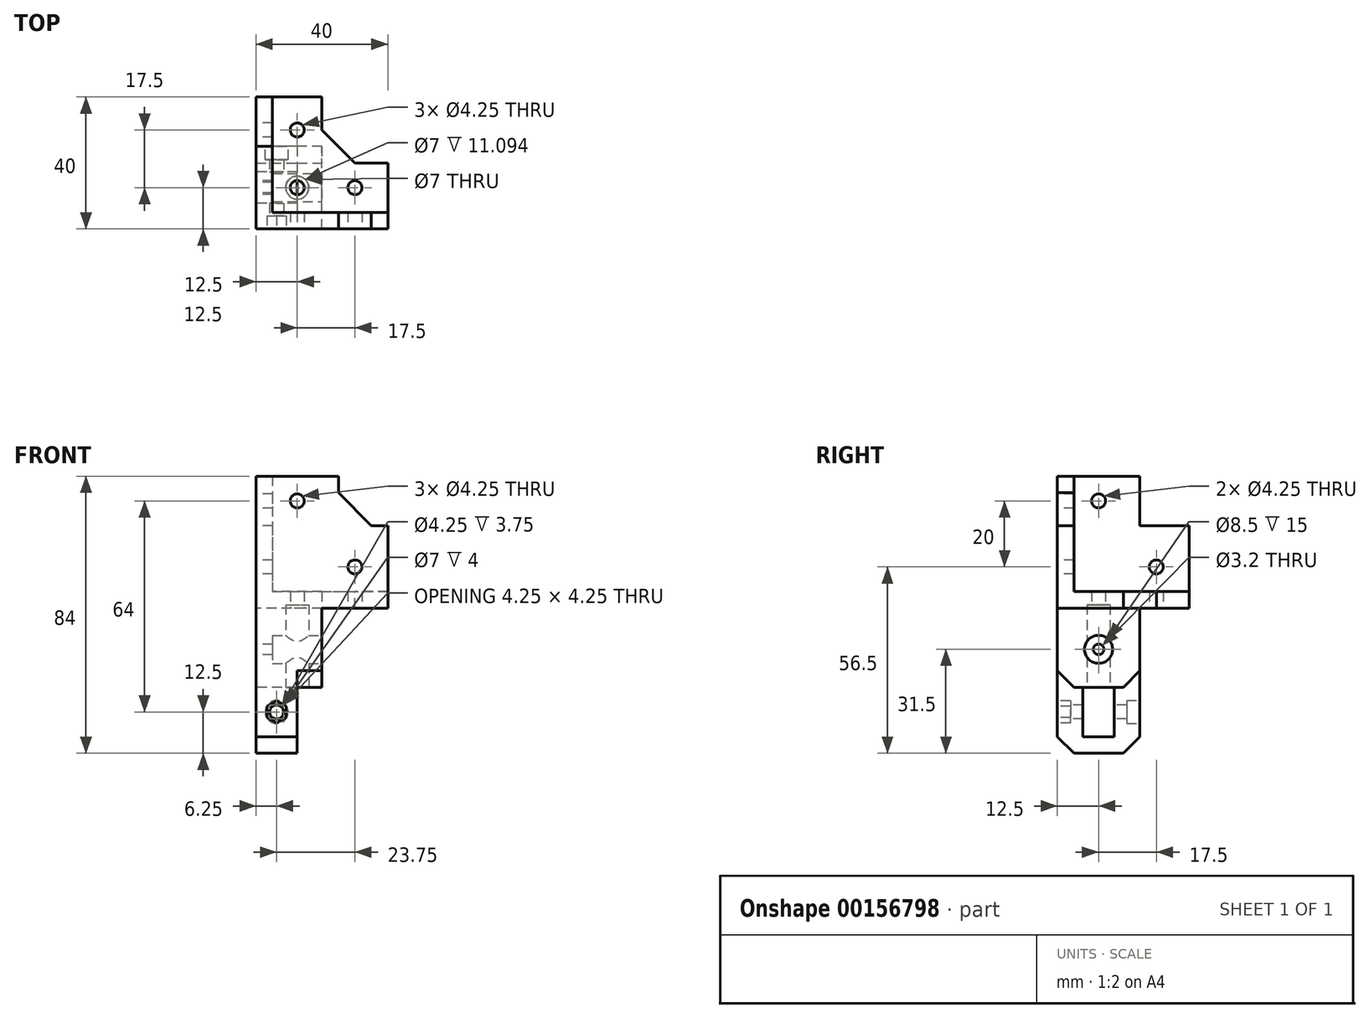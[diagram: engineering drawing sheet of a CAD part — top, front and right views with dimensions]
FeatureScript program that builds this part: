
annotation { "Feature Type Name" : "Feature", "Feature Type Description" : "" }
export const myFeature = defineFeature(function(context is Context, id is Id, definition is map)
    precondition{}
    {
        {
            var Q0;
            Q0=qCreatedBy(makeId("Top.planeOp"),FACE);
            var sketch = newSketch(context, id + "F0", { "sketchPlane" : qUnion([Q0])});
            skLineSegment(sketch, "E0", {"start": v(0, 40) * mm, "end": v(-20, 40) * mm});
            skLineSegment(sketch, "E1", {"start": v(-20, 40) * mm, "end": v(-20, 0) * mm});
            skLineSegment(sketch, "E2", {"start": v(-20, 0) * mm, "end": v(20, 0) * mm});
            skLineSegment(sketch, "E3", {"start": v(20, 0) * mm, "end": v(20, 20) * mm});
            skLineSegment(sketch, "E4", {"start": v(20, 20) * mm, "end": v(0, 20) * mm});
            skLineSegment(sketch, "E5", {"start": v(0, 20) * mm, "end": v(0, 40) * mm});
            skCircle(sketch, "E6", {"center": v(-7.5, 30) * mm, "radius": 2.12 * mm});
            skCircle(sketch, "E7", {"center": v(10, 12.5) * mm, "radius": 2.12 * mm});
            skCircle(sketch, "E8", {"center": v(-7.5, 12.5) * mm, "radius": 2.12 * mm});
            skSolve(sketch);
        }
        {
            var Q0;
            Q0=qSketchRegion(id+"F0",true);
            extrude(context, id + "F1", {"entities" : qUnion([Q0]), "depth" : 5 * mm});
        }
        {
            var Q0;
            Q0=makeQuery(id+"F1.opExtrude","CAP_FACE",FACE,{"disambiguationData":[OSD([sQuery(id+"F0.wireOp",EDGE,"E0"),sQuery(id+"F0.wireOp",EDGE,"E1"),sQuery(id+"F0.wireOp",EDGE,"E2"),sQuery(id+"F0.wireOp",EDGE,"E3"),sQuery(id+"F0.wireOp",EDGE,"E4"),sQuery(id+"F0.wireOp",EDGE,"E5"),sQuery(id+"F0.wireOp",EDGE,"E6"),sQuery(id+"F0.wireOp",EDGE,"E7")])],"isStart":false});
            var sketch = newSketch(context, id + "F2", { "sketchPlane" : qUnion([Q0])});
            skLineSegment(sketch, "E9", {"start": v(-20, 40) * mm, "end": v(-15, 40) * mm});
            skLineSegment(sketch, "E10", {"start": v(-15, 40) * mm, "end": v(-15, 5) * mm});
            skLineSegment(sketch, "E11", {"start": v(-15, 5) * mm, "end": v(20, 5) * mm});
            skLineSegment(sketch, "E12", {"start": v(20, 5) * mm, "end": v(20, 0) * mm});
            skLineSegment(sketch, "E13", {"start": v(20, 0) * mm, "end": v(-20, 0) * mm});
            skLineSegment(sketch, "E14", {"start": v(-20, 0) * mm, "end": v(-20, 40) * mm});
            skSolve(sketch);
        }
        {
            var Q0;
            Q0=qSketchRegion(id+"F2",true);
            extrude(context, id + "F3", {"entities" : qUnion([Q0]), "operationType" : NewBodyOperationType.ADD, "depth" : 20 * mm});
        }
        {
            var Q0;
            Q0=makeQuery(id+"F3.opExtrude","CAP_FACE",FACE,{"disambiguationData":[OSD([sQuery(id+"F2.wireOp",EDGE,"E9"),sQuery(id+"F2.wireOp",EDGE,"E10"),sQuery(id+"F2.wireOp",EDGE,"E11"),sQuery(id+"F2.wireOp",EDGE,"E12"),sQuery(id+"F2.wireOp",EDGE,"E13"),sQuery(id+"F2.wireOp",EDGE,"E14")])],"isStart":false});
            var sketch = newSketch(context, id + "F4", { "sketchPlane" : qUnion([Q0])});
            skLineSegment(sketch, "E15", {"start": v(-15, 25) * mm, "end": v(-20, 25) * mm});
            skLineSegment(sketch, "E16", {"start": v(-20, 25) * mm, "end": v(-20, 0) * mm});
            skLineSegment(sketch, "E17", {"start": v(-20, 0) * mm, "end": v(5, 0) * mm});
            skLineSegment(sketch, "E18", {"start": v(5, 0) * mm, "end": v(5, 5) * mm});
            skLineSegment(sketch, "E19", {"start": v(5, 5) * mm, "end": v(-15, 5) * mm});
            skLineSegment(sketch, "E20", {"start": v(-15, 5) * mm, "end": v(-15, 25) * mm});
            skSolve(sketch);
        }
        {
            var Q0;
            Q0=qSketchRegion(id+"F4",true);
            extrude(context, id + "F5", {"entities" : qUnion([Q0]), "operationType" : NewBodyOperationType.ADD, "depth" : 15 * mm});
        }
        {
            var Q0;
            Q0=makeQuery(id+"F1.opExtrude","SWEPT_EDGE",EDGE,{"disambiguationData":[OSD([sQuery(id+"F0.wireOp",EDGE,"E4"),sQuery(id+"F0.wireOp",EDGE,"E5")])]});
            var Q1;
            Q1=makeQuery(id+"F5.opExtrude","CAP_EDGE",EDGE,{"disambiguationData":[OSD([sQuery(id+"F4.wireOp",EDGE,"E15")])],"isStart":true});
            var Q2;
            Q2=makeQuery(id+"F5.opExtrude","CAP_EDGE",EDGE,{"disambiguationData":[OSD([sQuery(id+"F4.wireOp",EDGE,"E18")])],"isStart":true});
            chamfer(context, id + "F6", {"entities" : qUnion([Q0, Q1, Q2]), "width" : 10 * mm, "tangentPropagation" : true});
        }
        {
            var Q0;
            Q0=makeQuery(id+"F5.boolean.opBoolean","MERGE",FACE,{"derivedFrom":[makeQuery(id+"F3.boolean.opBoolean","MERGE",FACE,{"derivedFrom":[makeQuery(id+"F1.opExtrude","SWEPT_FACE",FACE,{"disambiguationData":[OSD([sQuery(id+"F0.wireOp",EDGE,"E2")])]}),makeQuery(id+"F3.opExtrude","SWEPT_FACE",FACE,{"disambiguationData":[OSD([sQuery(id+"F2.wireOp",EDGE,"E13")])]})]}),makeQuery(id+"F5.opExtrude","SWEPT_FACE",FACE,{"disambiguationData":[OSD([sQuery(id+"F4.wireOp",EDGE,"E17")])]})]});
            var sketch = newSketch(context, id + "F7", { "sketchPlane" : qUnion([Q0])});
            skCircle(sketch, "E21", {"center": v(-7.5, 32.5) * mm, "radius": 2.12 * mm});
            skCircle(sketch, "E22", {"center": v(10, 12.5) * mm, "radius": 2.12 * mm});
            skSolve(sketch);
        }
        {
            var Q0;
            Q0=qSketchRegion(id+"F7",true);
            extrude(context, id + "F8", {"entities" : qUnion([Q0]), "operationType" : NewBodyOperationType.REMOVE, "oppositeDirection" : true, "depth" : 5 * mm});
        }
        {
            var Q0;
            Q0=makeQuery(id+"F5.boolean.opBoolean","MERGE",FACE,{"derivedFrom":[makeQuery(id+"F3.boolean.opBoolean","MERGE",FACE,{"derivedFrom":[makeQuery(id+"F1.opExtrude","SWEPT_FACE",FACE,{"disambiguationData":[OSD([sQuery(id+"F0.wireOp",EDGE,"E1")])]}),makeQuery(id+"F3.opExtrude","SWEPT_FACE",FACE,{"disambiguationData":[OSD([sQuery(id+"F2.wireOp",EDGE,"E14")])]})]}),makeQuery(id+"F5.opExtrude","SWEPT_FACE",FACE,{"disambiguationData":[OSD([sQuery(id+"F4.wireOp",EDGE,"E16")])]})]});
            var sketch = newSketch(context, id + "F9", { "sketchPlane" : qUnion([Q0])});
            skCircle(sketch, "E23", {"center": v(-12.5, 32.5) * mm, "radius": 2.12 * mm});
            skCircle(sketch, "E24", {"center": v(-30, 12.5) * mm, "radius": 2.12 * mm});
            skSolve(sketch);
        }
        {
            var Q0;
            Q0=qSketchRegion(id+"F9",true);
            extrude(context, id + "F10", {"entities" : qUnion([Q0]), "operationType" : NewBodyOperationType.REMOVE, "oppositeDirection" : true, "depth" : 5 * mm});
        }
        {
            var Q0;
            Q0=makeQuery(id+"F1.opExtrude","CAP_FACE",FACE,{"disambiguationData":[OSD([sQuery(id+"F0.wireOp",EDGE,"E0"),sQuery(id+"F0.wireOp",EDGE,"E1"),sQuery(id+"F0.wireOp",EDGE,"E2"),sQuery(id+"F0.wireOp",EDGE,"E3"),sQuery(id+"F0.wireOp",EDGE,"E4"),sQuery(id+"F0.wireOp",EDGE,"E5"),sQuery(id+"F0.wireOp",EDGE,"E6"),sQuery(id+"F0.wireOp",EDGE,"E7"),sQuery(id+"F0.wireOp",EDGE,"E8")])],"isStart":true});
            var sketch = newSketch(context, id + "F11", { "sketchPlane" : qUnion([Q0])});
            skLineSegment(sketch, "E25.bottom", {"start": v(20, -20) * mm, "end": v(-20, -20) * mm});
            skLineSegment(sketch, "E25.top", {"start": v(20, 0) * mm, "end": v(-20, 0) * mm});
            skLineSegment(sketch, "E25.left", {"start": v(20, -20) * mm, "end": v(20, 0) * mm});
            skLineSegment(sketch, "E25.right", {"start": v(-20, -20) * mm, "end": v(-20, 0) * mm});
            skPoint(sketch, "E25.middle", {"position": v(0, -10) * mm});
            skPoint(sketch, "E26.visualSharp", {"position": v(-20, 0) * mm});
            skLineSegment(sketch, "E26.filletArc", {"start": v(-20, 0) * mm, "end": v(-20, 0) * mm});
            skCircle(sketch, "E27", {"center": v(10, -12.5) * mm, "radius": 2.12 * mm});
            skCircle(sketch, "E28", {"center": v(-7.5, -12.5) * mm, "radius": 2.12 * mm});
            skSolve(sketch);
        }
        {
            var Q0;
            Q0=qSketchRegion(id+"F11",true);
            extrude(context, id + "F12", {"entities" : qUnion([Q0]), "operationType" : NewBodyOperationType.ADD, "depth" : 24 * mm});
        }
        {
            var Q0;
            Q0=makeQuery(id+"F12.boolean.opBoolean","MERGE",FACE,{"derivedFrom":[makeQuery(id+"F1.opExtrude","SWEPT_FACE",FACE,{"disambiguationData":[OSD([sQuery(id+"F0.wireOp",EDGE,"E4")])]}),makeQuery(id+"F12.opExtrude","SWEPT_FACE",FACE,{"disambiguationData":[OSD([sQuery(id+"F11.wireOp",EDGE,"E25.bottom")])]})]});
            var sketch = newSketch(context, id + "F13", { "sketchPlane" : qUnion([Q0])});
            skLineSegment(sketch, "E29", {"start": v(20, -11.5) * mm, "end": v(20, -24) * mm});
            skLineSegment(sketch, "E30", {"start": v(20, -24) * mm, "end": v(7.5, -24) * mm});
            skPoint(sketch, "E31.orphan", {"position": v(7.5, -24) * mm});
            skCircle(sketch, "E32", {"center": v(7.5, -11.5) * mm, "radius": 4.15 * mm, "construction": true});
            skLineSegment(sketch, "E33", {"start": v(0, -11.5) * mm, "end": v(0, 0) * mm});
            skLineSegment(sketch, "E34", {"start": v(0, 0) * mm, "end": v(-20, 0) * mm});
            skLineSegment(sketch, "E35", {"start": v(-20, 0) * mm, "end": v(-20, -24) * mm});
            skLineSegment(sketch, "E36", {"start": v(-20, -24) * mm, "end": v(7.5, -24) * mm});
            skLineSegment(sketch, "E37", {"start": v(0, -11.5) * mm, "end": v(0, -24) * mm});
            skSolve(sketch);
        }
        {
            var Q0;
            Q0=qSketchRegion(id+"F13",true);
            extrude(context, id + "F14", {"entities" : qUnion([Q0]), "operationType" : NewBodyOperationType.REMOVE, "oppositeDirection" : true, "depth" : 25 * mm});
        }
        {
            var Q0;
            Q0=makeQuery(id+"F14.boolean.opBoolean","COPY",FACE,{"derivedFrom":makeQuery(id+"F14.opExtrude","SWEPT_FACE",FACE,{"disambiguationData":[OSD([sQuery(id+"F13.wireOp",EDGE,"E33"),sQuery(id+"F13.wireOp",EDGE,"E37")])]})});
            var sketch = newSketch(context, id + "F15", { "sketchPlane" : qUnion([Q0])});
            skCircle(sketch, "E38", {"center": v(12.5, -12.5) * mm, "radius": 4.25 * mm});
            skSolve(sketch);
        }
        {
            var Q0;
            Q0=qSketchRegion(id+"F15",true);
            extrude(context, id + "F16", {"entities" : qUnion([Q0]), "operationType" : NewBodyOperationType.REMOVE, "oppositeDirection" : true, "depth" : 20 * mm});
        }
        {
            var Q0;
            Q0=makeQuery(id+"F12.opExtrude","CAP_FACE",FACE,{"disambiguationData":[OSD([sQuery(id+"F11.wireOp",EDGE,"E25.bottom"),sQuery(id+"F11.wireOp",EDGE,"E25.top"),sQuery(id+"F11.wireOp",EDGE,"E25.left"),sQuery(id+"F11.wireOp",EDGE,"E25.right"),sQuery(id+"F11.wireOp",EDGE,"E27"),sQuery(id+"F11.wireOp",EDGE,"E28")])],"isStart":false});
            var sketch = newSketch(context, id + "F17", { "sketchPlane" : qUnion([Q0])});
            skCircle(sketch, "E39", {"center": v(-7.5, -12.5) * mm, "radius": 3.5 * mm});
            skSolve(sketch);
        }
        {
            var Q0;
            Q0=qSketchRegion(id+"F17",true);
            extrude(context, id + "F18", {"entities" : qUnion([Q0]), "operationType" : NewBodyOperationType.REMOVE, "oppositeDirection" : true, "depth" : 25 * mm});
        }
        {
            var Q0;
            {var subQ1=sQuery(id+"F11.wireOp",EDGE,"E25.bottom");var subQ2=sQuery(id+"F0.wireOp",EDGE,"E1");var subQ3=sQuery(id+"F0.wireOp",EDGE,"E4");Q0=makeQuery(id+"F14.boolean.opBoolean","SPLIT",FACE,{"disambiguationData":[TD([makeQuery(id+"F1.opExtrude","SWEPT_FACE",FACE,{"disambiguationData":[OSD([subQ2])]})])],"derivedFrom":makeQuery(id+"F12.boolean.opBoolean","MERGE",FACE,{"derivedFrom":[makeQuery(id+"F1.opExtrude","SWEPT_FACE",FACE,{"disambiguationData":[OSD([subQ3])]}),makeQuery(id+"F12.opExtrude","SWEPT_FACE",FACE,{"disambiguationData":[OSD([subQ1])]})]})});}
            var sketch = newSketch(context, id + "F19", { "sketchPlane" : qUnion([Q0])});
            skLineSegment(sketch, "E40.bottom", {"start": v(0, 0) * mm, "end": v(20, 0) * mm});
            skLineSegment(sketch, "E40.top", {"start": v(0, -24) * mm, "end": v(20, -24) * mm});
            skLineSegment(sketch, "E40.left", {"start": v(0, 0) * mm, "end": v(0, -24) * mm});
            skLineSegment(sketch, "E40.right", {"start": v(20, 0) * mm, "end": v(20, -24) * mm});
            skSolve(sketch);
        }
        {
            var Q0;
            Q0=qSketchRegion(id+"F19",true);
            extrude(context, id + "F20", {"entities" : qUnion([Q0]), "operationType" : NewBodyOperationType.ADD, "depth" : 5 * mm});
        }
        {
            var Q0;
            Q0=makeQuery(id+"F20.boolean.opBoolean","MERGE",FACE,{"derivedFrom":[makeQuery(id+"F12.boolean.opBoolean","MERGE",FACE,{"derivedFrom":[makeQuery(id+"F5.boolean.opBoolean","MERGE",FACE,{"derivedFrom":[makeQuery(id+"F3.boolean.opBoolean","MERGE",FACE,{"derivedFrom":[makeQuery(id+"F1.opExtrude","SWEPT_FACE",FACE,{"disambiguationData":[OSD([sQuery(id+"F0.wireOp",EDGE,"E1")])]}),makeQuery(id+"F3.opExtrude","SWEPT_FACE",FACE,{"disambiguationData":[OSD([sQuery(id+"F2.wireOp",EDGE,"E14")])]})]}),makeQuery(id+"F5.opExtrude","SWEPT_FACE",FACE,{"disambiguationData":[OSD([sQuery(id+"F4.wireOp",EDGE,"E16")])]})]}),makeQuery(id+"F12.opExtrude","SWEPT_FACE",FACE,{"disambiguationData":[OSD([sQuery(id+"F11.wireOp",EDGE,"E25.right")])]})]}),makeQuery(id+"F20.opExtrude","SWEPT_FACE",FACE,{"disambiguationData":[OSD([sQuery(id+"F19.wireOp",EDGE,"E40.right")])]})]});
            var sketch = newSketch(context, id + "F21", { "sketchPlane" : qUnion([Q0])});
            skLineSegment(sketch, "E41", {"start": v(-25, -24) * mm, "end": v(-25, -44) * mm});
            skLineSegment(sketch, "E42", {"start": v(-25, -44) * mm, "end": v(0, -44) * mm});
            skLineSegment(sketch, "E43", {"start": v(0, -44) * mm, "end": v(0, -24) * mm});
            skLineSegment(sketch, "E44", {"start": v(0, -24) * mm, "end": v(-7.75, -24) * mm});
            skLineSegment(sketch, "E45", {"start": v(-7.75, -24) * mm, "end": v(-7.75, -39) * mm});
            skLineSegment(sketch, "E46", {"start": v(-7.75, -39) * mm, "end": v(-17.25, -39) * mm});
            skLineSegment(sketch, "E47", {"start": v(-17.25, -39) * mm, "end": v(-17.25, -24) * mm});
            skLineSegment(sketch, "E48", {"start": v(-17.25, -24) * mm, "end": v(-25, -24) * mm});
            skSolve(sketch);
        }
        {
            var Q0;
            Q0=qSketchRegion(id+"F21",true);
            extrude(context, id + "F22", {"entities" : qUnion([Q0]), "operationType" : NewBodyOperationType.ADD, "oppositeDirection" : true, "depth" : 12.5 * mm});
        }
        {
            var Q0;
            Q0=makeQuery(id+"F22.opExtrude","SWEPT_EDGE",EDGE,{"disambiguationData":[OSD([sQuery(id+"F21.wireOp",EDGE,"E41"),sQuery(id+"F21.wireOp",EDGE,"E42")])]});
            var Q1;
            Q1=makeQuery(id+"F22.opExtrude","SWEPT_EDGE",EDGE,{"disambiguationData":[OSD([sQuery(id+"F21.wireOp",EDGE,"E42"),sQuery(id+"F21.wireOp",EDGE,"E43")])]});
            var Q2;
            Q2=makeQuery(id+"F12.opExtrude","CAP_EDGE",EDGE,{"disambiguationData":[OSD([sQuery(id+"F11.wireOp",EDGE,"E25.top")])],"isStart":false});
            var Q3;
            Q3=makeQuery(id+"F20.opExtrude","CAP_EDGE",EDGE,{"disambiguationData":[OSD([sQuery(id+"F19.wireOp",EDGE,"E40.top")])],"isStart":false});
            var Q4;
            Q4=makeQuery(id+"F20.opExtrude","CAP_EDGE",EDGE,{"disambiguationData":[OSD([sQuery(id+"F19.wireOp",EDGE,"E40.bottom")])],"isStart":false});
            chamfer(context, id + "F23", {"entities" : qUnion([Q0, Q1, Q2, Q3, Q4]), "width" : 5 * mm, "tangentPropagation" : true});
        }
        {
            var Q0;
            Q0=makeQuery(id+"F23.opChamfer","SPLIT",FACE,{"disambiguationData":[OD(1.0)],"derivedFrom":makeQuery(id+"F14.boolean.opBoolean","MERGE",FACE,{"derivedFrom":[makeQuery(id+"F1.opExtrude","CAP_FACE",FACE,{"disambiguationData":[OSD([sQuery(id+"F0.wireOp",EDGE,"E0"),sQuery(id+"F0.wireOp",EDGE,"E1"),sQuery(id+"F0.wireOp",EDGE,"E2"),sQuery(id+"F0.wireOp",EDGE,"E3"),sQuery(id+"F0.wireOp",EDGE,"E4"),sQuery(id+"F0.wireOp",EDGE,"E5"),sQuery(id+"F0.wireOp",EDGE,"E6"),sQuery(id+"F0.wireOp",EDGE,"E7"),sQuery(id+"F0.wireOp",EDGE,"E8")])],"isStart":true}),makeQuery(id+"F14.opExtrude","SWEPT_FACE",FACE,{"disambiguationData":[OSD([sQuery(id+"F13.wireOp",EDGE,"E34")])]})]})});
            var sketch = newSketch(context, id + "F24", { "sketchPlane" : qUnion([Q0])});
            skCircle(sketch, "E49", {"center": v(-7.5, -30) * mm, "radius": 3.5 * mm});
            skSolve(sketch);
        }
        {
            var Q0;
            Q0=qSketchRegion(id+"F24",true);
            extrude(context, id + "F25", {"entities" : qUnion([Q0]), "operationType" : NewBodyOperationType.REMOVE, "endBound" : BoundingType.THROUGH_ALL, "depth" : 25 * mm});
        }
        {
            var Q0;
            Q0=makeQuery(id+"F22.boolean.opBoolean","MERGE",FACE,{"derivedFrom":[makeQuery(id+"F20.boolean.opBoolean","MERGE",FACE,{"derivedFrom":[makeQuery(id+"F12.boolean.opBoolean","MERGE",FACE,{"derivedFrom":[makeQuery(id+"F5.boolean.opBoolean","MERGE",FACE,{"derivedFrom":[makeQuery(id+"F3.boolean.opBoolean","MERGE",FACE,{"derivedFrom":[makeQuery(id+"F1.opExtrude","SWEPT_FACE",FACE,{"disambiguationData":[OSD([sQuery(id+"F0.wireOp",EDGE,"E1")])]}),makeQuery(id+"F3.opExtrude","SWEPT_FACE",FACE,{"disambiguationData":[OSD([sQuery(id+"F2.wireOp",EDGE,"E14")])]})]}),makeQuery(id+"F5.opExtrude","SWEPT_FACE",FACE,{"disambiguationData":[OSD([sQuery(id+"F4.wireOp",EDGE,"E16")])]})]}),makeQuery(id+"F12.opExtrude","SWEPT_FACE",FACE,{"disambiguationData":[OSD([sQuery(id+"F11.wireOp",EDGE,"E25.right")])]})]}),makeQuery(id+"F20.opExtrude","SWEPT_FACE",FACE,{"disambiguationData":[OSD([sQuery(id+"F19.wireOp",EDGE,"E40.right")])]})]}),makeQuery(id+"F22.opExtrude","CAP_FACE",FACE,{"disambiguationData":[OSD([sQuery(id+"F21.wireOp",EDGE,"E41"),sQuery(id+"F21.wireOp",EDGE,"E42"),sQuery(id+"F21.wireOp",EDGE,"E43"),sQuery(id+"F21.wireOp",EDGE,"E44"),sQuery(id+"F21.wireOp",EDGE,"E45"),sQuery(id+"F21.wireOp",EDGE,"E46"),sQuery(id+"F21.wireOp",EDGE,"E47"),sQuery(id+"F21.wireOp",EDGE,"E48")])],"isStart":true})]});
            var sketch = newSketch(context, id + "F26", { "sketchPlane" : qUnion([Q0])});
            skCircle(sketch, "E50", {"center": v(-12.5, -12.5) * mm, "radius": 4.25 * mm});
            skCircle(sketch, "E51", {"center": v(-12.5, -12.5) * mm, "radius": 1.6 * mm});
            skSolve(sketch);
        }
        {
            var Q0;
            Q0=qSketchRegion(id+"F26",true);
            extrude(context, id + "F27", {"entities" : qUnion([Q0]), "operationType" : NewBodyOperationType.ADD, "oppositeDirection" : true, "depth" : 5 * mm});
        }
        {
            var Q0;
            Q0=makeQuery(id+"F22.boolean.opBoolean","MERGE",FACE,{"derivedFrom":[makeQuery(id+"F12.boolean.opBoolean","MERGE",FACE,{"derivedFrom":[makeQuery(id+"F5.boolean.opBoolean","MERGE",FACE,{"derivedFrom":[makeQuery(id+"F3.boolean.opBoolean","MERGE",FACE,{"derivedFrom":[makeQuery(id+"F1.opExtrude","SWEPT_FACE",FACE,{"disambiguationData":[OSD([sQuery(id+"F0.wireOp",EDGE,"E2")])]}),makeQuery(id+"F3.opExtrude","SWEPT_FACE",FACE,{"disambiguationData":[OSD([sQuery(id+"F2.wireOp",EDGE,"E13")])]})]}),makeQuery(id+"F5.opExtrude","SWEPT_FACE",FACE,{"disambiguationData":[OSD([sQuery(id+"F4.wireOp",EDGE,"E17")])]})]}),makeQuery(id+"F12.opExtrude","SWEPT_FACE",FACE,{"disambiguationData":[OSD([sQuery(id+"F11.wireOp",EDGE,"E25.top")])]})]}),makeQuery(id+"F22.opExtrude","SWEPT_FACE",FACE,{"disambiguationData":[OSD([sQuery(id+"F21.wireOp",EDGE,"E43")])]})]});
            var sketch = newSketch(context, id + "F28", { "sketchPlane" : qUnion([Q0])});
            skCircle(sketch, "E52", {"center": v(-13.75, -31.5) * mm, "radius": 2.12 * mm});
            skSolve(sketch);
        }
        {
            var Q0;
            Q0=qSketchRegion(id+"F28",true);
            extrude(context, id + "F29", {"entities" : qUnion([Q0]), "operationType" : NewBodyOperationType.REMOVE, "endBound" : BoundingType.THROUGH_ALL, "oppositeDirection" : true, "depth" : 25 * mm});
        }
        {
            var Q0;
            Q0=makeQuery(id+"F22.boolean.opBoolean","MERGE",FACE,{"derivedFrom":[makeQuery(id+"F12.boolean.opBoolean","MERGE",FACE,{"derivedFrom":[makeQuery(id+"F5.boolean.opBoolean","MERGE",FACE,{"derivedFrom":[makeQuery(id+"F3.boolean.opBoolean","MERGE",FACE,{"derivedFrom":[makeQuery(id+"F1.opExtrude","SWEPT_FACE",FACE,{"disambiguationData":[OSD([sQuery(id+"F0.wireOp",EDGE,"E2")])]}),makeQuery(id+"F3.opExtrude","SWEPT_FACE",FACE,{"disambiguationData":[OSD([sQuery(id+"F2.wireOp",EDGE,"E13")])]})]}),makeQuery(id+"F5.opExtrude","SWEPT_FACE",FACE,{"disambiguationData":[OSD([sQuery(id+"F4.wireOp",EDGE,"E17")])]})]}),makeQuery(id+"F12.opExtrude","SWEPT_FACE",FACE,{"disambiguationData":[OSD([sQuery(id+"F11.wireOp",EDGE,"E25.top")])]})]}),makeQuery(id+"F22.opExtrude","SWEPT_FACE",FACE,{"disambiguationData":[OSD([sQuery(id+"F21.wireOp",EDGE,"E43")])]})]});
            var sketch = newSketch(context, id + "F30", { "sketchPlane" : qUnion([Q0])});
            skCircle(sketch, "E53.cCircle", {"center": v(-13.75, -31.5) * mm, "radius": 2.93 * mm, "construction": true});
            skLineSegment(sketch, "E53.0", {"start": v(-10.82, -29.81) * mm, "end": v(-10.82, -33.19) * mm});
            skLineSegment(sketch, "E53.1", {"start": v(-10.82, -33.19) * mm, "end": v(-13.75, -34.88) * mm});
            skLineSegment(sketch, "E53.2", {"start": v(-13.75, -34.88) * mm, "end": v(-16.67, -33.19) * mm});
            skLineSegment(sketch, "E53.3", {"start": v(-16.67, -33.19) * mm, "end": v(-16.67, -29.81) * mm});
            skLineSegment(sketch, "E53.4", {"start": v(-16.67, -29.81) * mm, "end": v(-13.75, -28.12) * mm});
            skLineSegment(sketch, "E53.5", {"start": v(-13.75, -28.12) * mm, "end": v(-10.82, -29.81) * mm});
            skPoint(sketch, "E53.0.midPoint", {"position": v(-10.82, -31.5) * mm});
            skPoint(sketch, "E54.0.midPoint", {"position": v(-7.5, -31.5) * mm});
            skSolve(sketch);
        }
        {
            var Q0;
            Q0=qSketchRegion(id+"F30",true);
            extrude(context, id + "F31", {"entities" : qUnion([Q0]), "operationType" : NewBodyOperationType.REMOVE, "oppositeDirection" : true, "depth" : 4 * mm});
        }
        {
            var Q0;
            Q0=makeQuery(id+"F22.boolean.opBoolean","MERGE",FACE,{"derivedFrom":[makeQuery(id+"F20.opExtrude","CAP_FACE",FACE,{"disambiguationData":[OSD([sQuery(id+"F19.wireOp",EDGE,"E40.bottom"),sQuery(id+"F19.wireOp",EDGE,"E40.top"),sQuery(id+"F19.wireOp",EDGE,"E40.left"),sQuery(id+"F19.wireOp",EDGE,"E40.right")])],"isStart":false}),makeQuery(id+"F22.opExtrude","SWEPT_FACE",FACE,{"disambiguationData":[OSD([sQuery(id+"F21.wireOp",EDGE,"E41")])]})]});
            var sketch = newSketch(context, id + "F32", { "sketchPlane" : qUnion([Q0])});
            skCircle(sketch, "E55", {"center": v(13.75, -31.5) * mm, "radius": 3.5 * mm});
            skSolve(sketch);
        }
        {
            var Q0;
            Q0=qSketchRegion(id+"F32",true);
            extrude(context, id + "F33", {"entities" : qUnion([Q0]), "operationType" : NewBodyOperationType.REMOVE, "oppositeDirection" : true, "depth" : 4 * mm});
        }
    });
